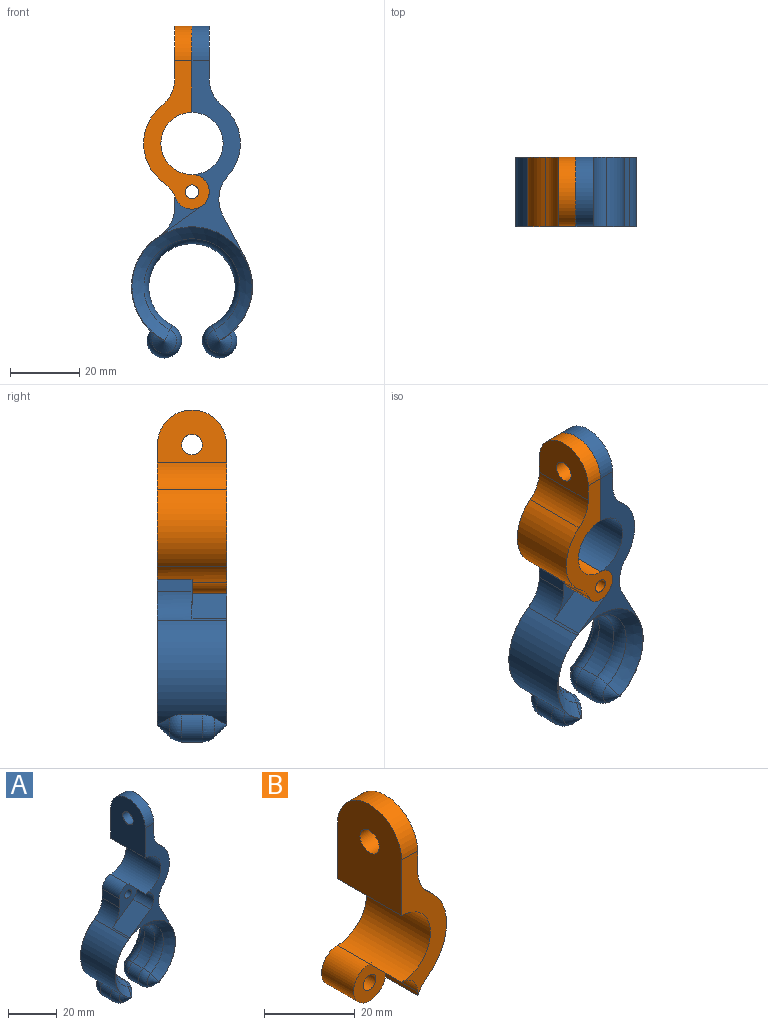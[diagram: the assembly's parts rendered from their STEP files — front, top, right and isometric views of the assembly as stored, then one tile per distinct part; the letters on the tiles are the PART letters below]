
ASSEMBLY  parts=2 mates=1
PART A: 35 faces, bbox 35x20x96.1 mm
  f0: cylinder r=5mm len=10mm, axis (0,1,0), area 78.5mm2, adj f1,f7,f17,f20
  f1: plane 10x4.45mm, normal (-1,0,0), area 44.5mm2, adj f0,f8,f17,f20
  f2: cylinder r=2mm len=10mm, axis (0,1,0), area 125.7mm2, adj f17,f20
  f3: plane 81.16x35mm, normal (0,-1,0), area 332.1mm2, adj f4,f5,f6,f7,f8,f9,f13,f14
  f4: cylinder r=10mm len=20mm, axis (0,1,0), area 179.1mm2, adj f3,f5,f16,f17
  f5: plane 20x15.27mm, normal (1,0,0), area 234.1mm2, adj f3,f4,f17,f21,f22
  f6: plane 25x20mm, normal (-1,0,0), area 428.8mm2, adj f3,f7,f17,f21,f22
  f7: cylinder r=9mm len=20mm, axis (0,1,0), area 565.5mm2, adj f0,f3,f6,f17,f19
  f8: cylinder r=10mm len=20mm, axis (0,1,0), area 106.7mm2, adj f1,f3,f9,f17,f18,f20
  f9: cylinder r=17.5mm len=30.19mm, axis (0,1,0), area 656.3mm2, adj f3,f8,f10,f17,f23,f26,f29,f34
  f10: cylinder r=5mm len=10mm, axis (0,1,0), area 147.1mm2, adj f9,f11,f29,f34
  f11: cylinder r=12.5mm len=25mm, axis (0,1,0), area 403.9mm2, adj f10,f12,f30,f33
  f12: cylinder r=5mm len=10mm, axis (0,1,0), area 147.1mm2, adj f11,f13,f31,f32
  f13: cylinder r=17.5mm len=23.62mm, axis (0,1,0), area 476.9mm2, adj f3,f12,f14,f17,f25,f28,f31,f32
  f14: plane 20x12.65mm, normal (0.89,0,0.46), area 285.4mm2, adj f3,f13,f15,f17
  f15: cylinder r=10mm len=20mm, axis (0,1,0), area 243.6mm2, adj f3,f14,f16,f17
  f16: cylinder r=14mm len=20.34mm, axis (0,1,0), area 457.1mm2, adj f3,f4,f15,f17
  f17: plane 81.16x35mm, normal (0,1,0), area 422.9mm2, adj f0,f1,f2,f4,f5,f6,f7,f8
  f18: plane 11.83x10mm, normal (-0.58,0,0.82), area 144.6mm2, adj f3,f8,f19,f20
  f19: cylinder r=5mm len=10mm, axis (0,-1,0), area 126.4mm2, adj f3,f7,f18,f20
  f20: plane 17.41x13.95mm, normal (0,-1,0), area 90.8mm2, adj f0,f1,f2,f8,f18,f19
  f21: cylinder r=10mm len=20mm, axis (1,0,0), area 157.1mm2, adj f3,f5,f6,f17
  f22: cylinder r=3mm len=6mm, axis (1,0,0), area 94.2mm2, adj f5,f6
  f23: cone r=5mm half-angle=45deg, axis (0,1,0), area 42.2mm2, adj f3,f9,f24,f29
  f24: cone r=12.5mm half-angle=45deg, axis (0,-1,0), area 406.4mm2, adj f3,f23,f25,f30
  f25: cone r=0.1mm half-angle=45deg, axis (0,1,0), area 42.2mm2, adj f3,f13,f24,f31
  f26: cone r=0.1mm half-angle=45deg, axis (0,-1,0), area 42.2mm2, adj f9,f17,f27,f34
  f27: cone r=17.4mm half-angle=45deg, axis (0,1,0), area 406.4mm2, adj f17,f26,f28,f33
  f28: cone r=5mm half-angle=45deg, axis (0,-1,0), area 42.2mm2, adj f13,f17,f27,f32
  f29: sphere r=5mm, area 85.6mm2, adj f9,f10,f23,f30
  f30: torus R=17.5mm, axis (0,1,0), area 272.3mm2, adj f11,f24,f29,f31
  f31: sphere r=5mm, area 85.6mm2, adj f12,f13,f25,f30
  f32: sphere r=5mm, area 85.6mm2, adj f12,f13,f28,f33
  f33: torus R=17.5mm, axis (0,-1,0), area 272.3mm2, adj f11,f27,f32,f34
  f34: sphere r=5mm, area 85.6mm2, adj f9,f10,f26,f33
PART B: 15 faces, bbox 19x20x53 mm
  f0: cylinder r=5mm len=10mm, axis (0,1,0), area 216.7mm2, adj f1,f5,f9,f14
  f1: cylinder r=10mm len=20mm, axis (0,1,0), area 106mm2, adj f0,f3,f6,f9,f12,f14
  f2: cylinder r=2mm len=10mm, axis (0,1,0), area 125.7mm2, adj f9,f14
  f3: plane 39.06x14mm, normal (0,-1,0), area 220.3mm2, adj f1,f4,f5,f6,f7,f8,f10,f12
  f4: plane 25x20mm, normal (-1,0,0), area 428.8mm2, adj f3,f5,f9,f10,f11
  f5: cylinder r=9mm len=20mm, axis (0,1,0), area 565.5mm2, adj f0,f3,f4,f9,f13
  f6: cylinder r=14mm len=22.32mm, axis (0,1,0), area 517.1mm2, adj f1,f3,f7,f9
  f7: cylinder r=10mm len=20mm, axis (0,1,0), area 179.1mm2, adj f3,f6,f8,f9
  f8: plane 20x15.27mm, normal (1,0,0), area 234.1mm2, adj f3,f7,f9,f10,f11
  f9: plane 43x19mm, normal (0,1,0), area 286.3mm2, adj f0,f1,f2,f4,f5,f6,f7,f8
  f10: cylinder r=10mm len=20mm, axis (1,0,0), area 157.1mm2, adj f3,f4,f8,f9
  f11: cylinder r=3mm len=6mm, axis (1,0,0), area 94.2mm2, adj f4,f8
  f12: plane 10x1.06mm, normal (-1,0,0), area 10.6mm2, adj f1,f3,f13,f14
  f13: cylinder r=5mm len=10mm, axis (0,-1,0), area 78.5mm2, adj f3,f5,f12,f14
  f14: plane 10x10mm, normal (0,-1,0), area 66mm2, adj f0,f1,f2,f12,f13
PLACE A t=(-51.74,-46.24,-14.2)mm
PLACE B rot(axis=(0,0,1),180deg) t=(-51.74,-66.24,-2.29)mm
MATE revolute A.f0 <-> B.f2  axis (0,-1,0) through (-51.74,-56.24,-16.29)mm
